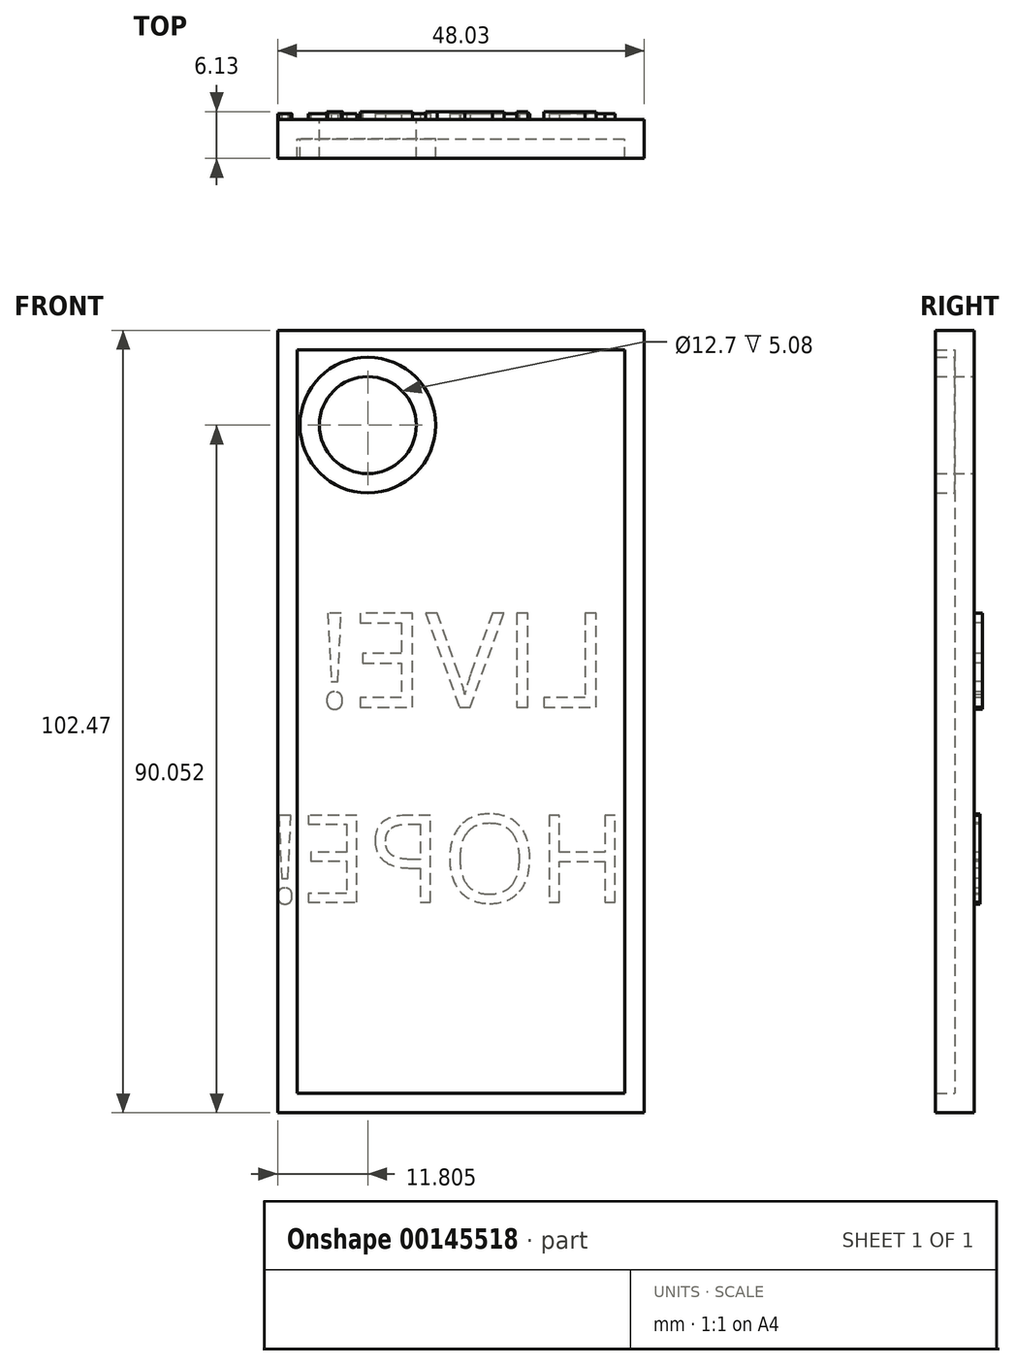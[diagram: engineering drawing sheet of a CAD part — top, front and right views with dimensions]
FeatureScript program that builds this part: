
annotation { "Feature Type Name" : "Feature", "Feature Type Description" : "" }
export const myFeature = defineFeature(function(context is Context, id is Id, definition is map)
    precondition{}
    {
        {
            var Q0;
            Q0=qCreatedBy(makeId("Front.planeOp"),FACE);
            var sketch = newSketch(context, id + "F0", { "sketchPlane" : qUnion([Q0])});
            skLineSegment(sketch, "E0.bottom", {"start": v(-24.94, 49.37) * mm, "end": v(23.08, 49.37) * mm});
            skLineSegment(sketch, "E0.top", {"start": v(-24.94, -53.1) * mm, "end": v(23.08, -53.1) * mm});
            skLineSegment(sketch, "E0.left", {"start": v(-24.94, 49.37) * mm, "end": v(-24.94, -53.1) * mm});
            skLineSegment(sketch, "E0.right", {"start": v(23.08, 49.37) * mm, "end": v(23.08, -53.1) * mm});
            skSolve(sketch);
        }
        {
            var Q0;
            Q0=makeQuery(id+"F0.imprint","IMPRINT",FACE,{"disambiguationData":[TD([[makeQuery(id+"F0.imprint","IMPRINT",EDGE,{"derivedFrom":sQuery(id+"F0.wireOp",EDGE,"E0.bottom")}),-1.0]])]});
            extrude(context, id + "F1", {"entities" : qUnion([Q0]), "depth" : 5.08 * mm});
        }
        {
            var Q0;
            Q0=makeQuery(id+"F1.opExtrude","CAP_FACE",FACE,{"disambiguationData":[OSD([sQuery(id+"F0.wireOp",EDGE,"E0.bottom"),sQuery(id+"F0.wireOp",EDGE,"E0.top"),sQuery(id+"F0.wireOp",EDGE,"E0.left"),sQuery(id+"F0.wireOp",EDGE,"E0.right")])],"isStart":true});
            var sketch = newSketch(context, id + "F2", { "sketchPlane" : qUnion([Q0])});
            skLineSegment(sketch, "E1", {"start": v(13.15, 49.37) * mm, "end": v(13.15, 36.95) * mm});
            skSolve(sketch);
        }
        {
            var Q0;
            Q0=sQuery(id+"F2.wireOp",VERTEX,"E1.end");
            var Q1;
            Q1=makeQuery(id+"F1.opExtrude","SWEPT_BODY",BODY,{"disambiguationData":[OSD([sQuery(id+"F0.wireOp",EDGE,"E0.bottom"),sQuery(id+"F0.wireOp",EDGE,"E0.top"),sQuery(id+"F0.wireOp",EDGE,"E0.left"),sQuery(id+"F0.wireOp",EDGE,"E0.right")])]});
            hole(context, id + "F3", {"style" : HoleStyle.SIMPLE, "endStyle" : HoleEndStyle.THROUGH, "holeDiameter" : 12.7 * mm, "startFromSketch" : true, "locations" : qUnion([Q0]), "scope" : qUnion([Q1]), "isTappedThrough" : true});
        }
        {
            var Q0;
            Q0=makeQuery(id+"F1.opExtrude","CAP_FACE",FACE,{"disambiguationData":[OSD([sQuery(id+"F0.wireOp",EDGE,"E0.bottom"),sQuery(id+"F0.wireOp",EDGE,"E0.top"),sQuery(id+"F0.wireOp",EDGE,"E0.left"),sQuery(id+"F0.wireOp",EDGE,"E0.right")])],"isStart":false});
            shell(context, id + "F4", {"entities" : qUnion([Q0]), "thickness" : 2.54 * mm});
        }
        {
            var Q0;
            Q0=makeQuery(id+"F1.opExtrude","CAP_FACE",FACE,{"disambiguationData":[OSD([sQuery(id+"F0.wireOp",EDGE,"E0.bottom"),sQuery(id+"F0.wireOp",EDGE,"E0.top"),sQuery(id+"F0.wireOp",EDGE,"E0.left"),sQuery(id+"F0.wireOp",EDGE,"E0.right")])],"isStart":true});
            var sketch = newSketch(context, id + "F5", { "sketchPlane" : qUnion([Q0])});
            skText(sketch, "E2", { "text": "LIVE!", "fontName": "OpenSans-Regular.ttf"});
            const initialGuessF5  = {"E2": [-0.01848, 0, 1, 0, 0.01244]};
            skSetInitialGuess(sketch, initialGuessF5);
            skSolve(sketch);
        }
        {
            var Q0;
            Q0 = qSketchRegion(id + "F5", true);
            extrude(context, id + "F6", {"entities" : qUnion([Q0]), "operationType" : NewBodyOperationType.ADD, "depth" : 1.05 * mm});
        }
        {
            var Q0;
            Q0=makeQuery(id+"F1.opExtrude","CAP_FACE",FACE,{"disambiguationData":[OSD([sQuery(id+"F0.wireOp",EDGE,"E0.bottom"),sQuery(id+"F0.wireOp",EDGE,"E0.top"),sQuery(id+"F0.wireOp",EDGE,"E0.left"),sQuery(id+"F0.wireOp",EDGE,"E0.right")])],"isStart":true});
            var sketch = newSketch(context, id + "F7", { "sketchPlane" : qUnion([Q0])});
            skText(sketch, "E3", { "text": "HOPE!\n", "fontName": "OpenSans-Regular.ttf"});
            const initialGuessF7  = {"E3": [-0.02084, -0.02553, 1, 0, 0.0115]};
            skSetInitialGuess(sketch, initialGuessF7);
            skSolve(sketch);
        }
        {
            var Q0;
            Q0 = qSketchRegion(id + "F7", true);
            extrude(context, id + "F8", {"entities" : qUnion([Q0]), "operationType" : NewBodyOperationType.ADD, "depth" : 0.76 * mm});
        }
    });
